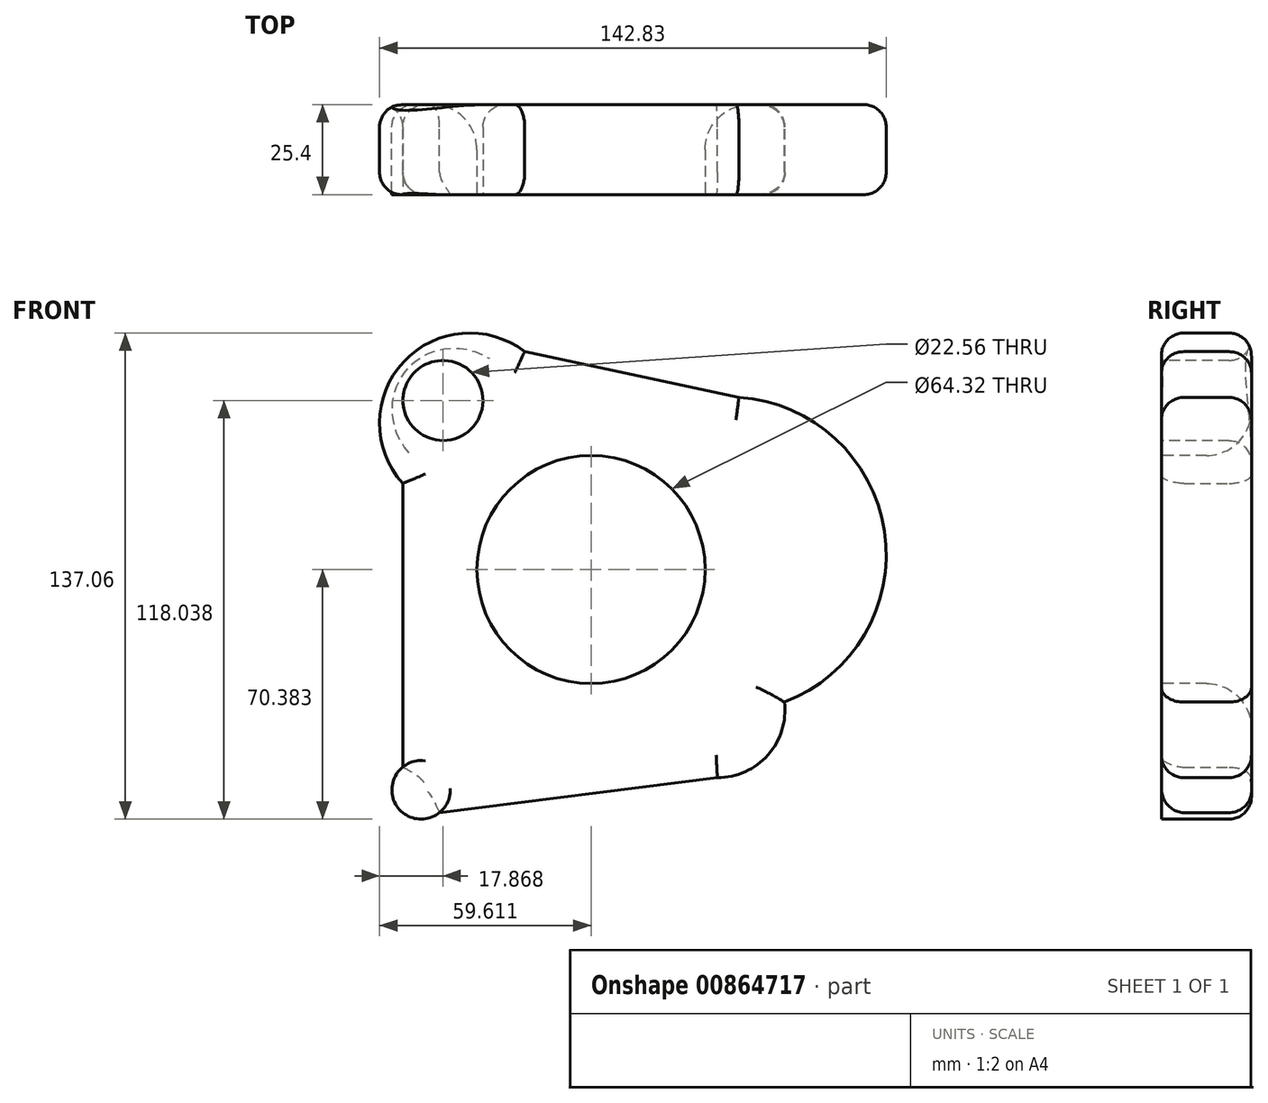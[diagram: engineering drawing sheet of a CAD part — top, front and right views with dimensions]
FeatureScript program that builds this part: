
annotation { "Feature Type Name" : "Feature", "Feature Type Description" : "" }
export const myFeature = defineFeature(function(context is Context, id is Id, definition is map)
    precondition{}
    {
        {
            var Q0;
            Q0=qCreatedBy(makeId("Front.planeOp"),FACE);
            var sketch = newSketch(context, id + "F0", { "sketchPlane" : qUnion([Q0])});
            skCircle(sketch, "E0", {"center": v(-53.98, 60.28) * mm, "radius": 25.4 * mm});
            skCircle(sketch, "E1", {"center": v(19, 23.17) * mm, "radius": 44.45 * mm});
            skCircle(sketch, "E2", {"center": v(-67.66, -43.13) * mm, "radius": 8.26 * mm});
            skCircle(sketch, "E3", {"center": v(15.86, -20.64) * mm, "radius": 19.05 * mm});
            skLineSegment(sketch, "E4", {"start": v(-38.48, 80.4) * mm, "end": v(34.4, 64.86) * mm});
            skLineSegment(sketch, "E5", {"start": v(60.44, 7.1) * mm, "end": v(15.86, -20.64) * mm});
            skLineSegment(sketch, "E6", {"start": v(15.86, -39.7) * mm, "end": v(-62.46, -49.54) * mm});
            skLineSegment(sketch, "E7", {"start": v(-72.86, 43.3) * mm, "end": v(-72.86, -36.72) * mm});
            skSolve(sketch);
        }
        {
            var Q0;
            Q0 = qSketchRegion(id + "F0", true);
            extrude(context, id + "F1", {"entities" : qUnion([Q0]), "depth" : 25.4 * mm, "offsetDistance" : 25.4 * mm});
        }
        {
            var Q0;
            Q0=makeQuery(id+"F1.opExtrude","CAP_FACE",FACE,{"disambiguationData":[OSD([sQuery(id+"F0.wireOp",EDGE,"E0"),sQuery(id+"F0.wireOp",EDGE,"E1"),sQuery(id+"F0.wireOp",EDGE,"E2"),sQuery(id+"F0.wireOp",EDGE,"E3"),sQuery(id+"F0.wireOp",EDGE,"E4"),sQuery(id+"F0.wireOp",EDGE,"E6"),sQuery(id+"F0.wireOp",EDGE,"E7")])],"isStart":false});
            var sketch = newSketch(context, id + "F2", { "sketchPlane" : qUnion([Q0])});
            skCircle(sketch, "E8", {"center": v(-61.51, 66.66) * mm, "radius": 11.28 * mm});
            skSolve(sketch);
        }
        {
            var Q0;
            Q0 = qSketchRegion(id + "F2", true);
            extrude(context, id + "F3", {"entities" : qUnion([Q0]), "operationType" : NewBodyOperationType.ADD, "depth" : 76.2 * mm, "offsetDistance" : 25.4 * mm});
        }
        {
            var Q0;
            Q0=makeQuery(id+"F3.opExtrude","CAP_FACE",FACE,{"disambiguationData":[OSD([sQuery(id+"F2.wireOp",EDGE,"E8")])],"isStart":false});
            extrude(context, id + "F4", {"entities" : qUnion([Q0]), "operationType" : NewBodyOperationType.REMOVE, "endBound" : BoundingType.THROUGH_ALL, "oppositeDirection" : true, "depth" : 25.4 * mm, "offsetDistance" : 25.4 * mm});
        }
        {
            var Q0;
            Q0=makeQuery(id+"Fvwkc0aiCjp0DBf_1.boolean.opBoolean","INTERSECT",EDGE,{"derivedFrom":[makeQuery(id+"F1.opExtrude","CAP_FACE",FACE,{"disambiguationData":[OSD([sQuery(id+"F0.wireOp",EDGE,"E0"),sQuery(id+"F0.wireOp",EDGE,"E1"),sQuery(id+"F0.wireOp",EDGE,"E2"),sQuery(id+"F0.wireOp",EDGE,"E3"),sQuery(id+"F0.wireOp",EDGE,"E4"),sQuery(id+"F0.wireOp",EDGE,"E6"),sQuery(id+"F0.wireOp",EDGE,"E7")])],"isStart":true}),makeQuery(id+"Fvwkc0aiCjp0DBf_1.opExtrude","SWEPT_FACE",FACE,{"disambiguationData":[OSD([sQuery(id+"FM4Ox1MiRYVjufH_1.wireOp",EDGE,"iZuMQ9Cg-E2lU-WlAJ-14QO-pkKDaHSdI4NP.left")])]})]});
            var Q1;
            Q1=makeQuery(id+"Fvwkc0aiCjp0DBf_1.boolean.opBoolean","INTERSECT",EDGE,{"derivedFrom":[makeQuery(id+"F1.opExtrude","CAP_FACE",FACE,{"disambiguationData":[OSD([sQuery(id+"F0.wireOp",EDGE,"E0"),sQuery(id+"F0.wireOp",EDGE,"E1"),sQuery(id+"F0.wireOp",EDGE,"E2"),sQuery(id+"F0.wireOp",EDGE,"E3"),sQuery(id+"F0.wireOp",EDGE,"E4"),sQuery(id+"F0.wireOp",EDGE,"E6"),sQuery(id+"F0.wireOp",EDGE,"E7")])],"isStart":true}),makeQuery(id+"Fvwkc0aiCjp0DBf_1.opExtrude","SWEPT_FACE",FACE,{"disambiguationData":[OSD([sQuery(id+"FM4Ox1MiRYVjufH_1.wireOp",EDGE,"iZuMQ9Cg-E2lU-WlAJ-14QO-pkKDaHSdI4NP.top")])]})]});
            var Q2;
            Q2=makeQuery(id+"F1.opExtrude","CAP_FACE",FACE,{"disambiguationData":[OSD([sQuery(id+"F0.wireOp",EDGE,"E0"),sQuery(id+"F0.wireOp",EDGE,"E1"),sQuery(id+"F0.wireOp",EDGE,"E2"),sQuery(id+"F0.wireOp",EDGE,"E3"),sQuery(id+"F0.wireOp",EDGE,"E4"),sQuery(id+"F0.wireOp",EDGE,"E6"),sQuery(id+"F0.wireOp",EDGE,"E7")])],"isStart":true});
            var Q3;
            Q3=makeQuery(id+"Fvwkc0aiCjp0DBf_1.boolean.opBoolean","INTERSECT",EDGE,{"derivedFrom":[makeQuery(id+"F1.opExtrude","CAP_FACE",FACE,{"disambiguationData":[OSD([sQuery(id+"F0.wireOp",EDGE,"E0"),sQuery(id+"F0.wireOp",EDGE,"E1"),sQuery(id+"F0.wireOp",EDGE,"E2"),sQuery(id+"F0.wireOp",EDGE,"E3"),sQuery(id+"F0.wireOp",EDGE,"E4"),sQuery(id+"F0.wireOp",EDGE,"E6"),sQuery(id+"F0.wireOp",EDGE,"E7")])],"isStart":true}),makeQuery(id+"Fvwkc0aiCjp0DBf_1.opExtrude","SWEPT_FACE",FACE,{"disambiguationData":[OSD([sQuery(id+"FM4Ox1MiRYVjufH_1.wireOp",EDGE,"iZuMQ9Cg-E2lU-WlAJ-14QO-pkKDaHSdI4NP.bottom")])]})]});
            var Q4;
            Q4=makeQuery(id+"Fvwkc0aiCjp0DBf_1.boolean.opBoolean","INTERSECT",EDGE,{"derivedFrom":[makeQuery(id+"F1.opExtrude","CAP_FACE",FACE,{"disambiguationData":[OSD([sQuery(id+"F0.wireOp",EDGE,"E0"),sQuery(id+"F0.wireOp",EDGE,"E1"),sQuery(id+"F0.wireOp",EDGE,"E2"),sQuery(id+"F0.wireOp",EDGE,"E3"),sQuery(id+"F0.wireOp",EDGE,"E4"),sQuery(id+"F0.wireOp",EDGE,"E6"),sQuery(id+"F0.wireOp",EDGE,"E7")])],"isStart":true}),makeQuery(id+"Fvwkc0aiCjp0DBf_1.opExtrude","SWEPT_FACE",FACE,{"disambiguationData":[OSD([sQuery(id+"FM4Ox1MiRYVjufH_1.wireOp",EDGE,"iZuMQ9Cg-E2lU-WlAJ-14QO-pkKDaHSdI4NP.right")])]})]});
            var Q5;
            Q5=makeQuery(id+"F1.opExtrude","CAP_EDGE",EDGE,{"disambiguationData":[OSD([sQuery(id+"F0.wireOp",EDGE,"E6")])],"isStart":false});
            var Q6;
            Q6=makeQuery(id+"F1.opExtrude","CAP_EDGE",EDGE,{"disambiguationData":[OSD([sQuery(id+"F0.wireOp",EDGE,"E3")])],"isStart":false});
            var Q7;
            Q7=makeQuery(id+"F1.opExtrude","CAP_EDGE",EDGE,{"disambiguationData":[OSD([sQuery(id+"F0.wireOp",EDGE,"E1")])],"isStart":false});
            var Q8;
            Q8=makeQuery(id+"F1.opExtrude","CAP_EDGE",EDGE,{"disambiguationData":[OSD([sQuery(id+"F0.wireOp",EDGE,"E4")])],"isStart":false});
            var Q9;
            Q9=makeQuery(id+"F1.opExtrude","CAP_EDGE",EDGE,{"disambiguationData":[OSD([sQuery(id+"F0.wireOp",EDGE,"E0")])],"isStart":false});
            var Q10;
            Q10=makeQuery(id+"F1.opExtrude","CAP_EDGE",EDGE,{"disambiguationData":[OSD([sQuery(id+"F0.wireOp",EDGE,"E7")])],"isStart":false});
            var Q11;
            Q11=makeQuery(id+"F3.opExtrude","CAP_EDGE",EDGE,{"disambiguationData":[OSD([sQuery(id+"F2.wireOp",EDGE,"E8")])],"isStart":true});
            fillet(context, id + "F5", {"entities" : qUnion([Q0, Q1, Q2, Q3, Q4, Q5, Q6, Q7, Q8, Q9, Q10, Q11]), "radius" : 6.35 * mm, "tangentPropagation" : true, "allowEdgeOverflow" : false});
        }
        {
            var Q0;
            Q0=makeQuery(id+"F1.opExtrude","CAP_FACE",FACE,{"disambiguationData":[OSD([sQuery(id+"F0.wireOp",EDGE,"E0"),sQuery(id+"F0.wireOp",EDGE,"E1"),sQuery(id+"F0.wireOp",EDGE,"E2"),sQuery(id+"F0.wireOp",EDGE,"E3"),sQuery(id+"F0.wireOp",EDGE,"E4"),sQuery(id+"F0.wireOp",EDGE,"E6"),sQuery(id+"F0.wireOp",EDGE,"E7")])],"isStart":false});
            var sketch = newSketch(context, id + "F6", { "sketchPlane" : qUnion([Q0])});
            skCircle(sketch, "E9", {"center": v(-19.77, 19) * mm, "radius": 32.16 * mm});
            skSolve(sketch);
        }
        {
            var Q0;
            Q0=makeQuery(id+"F6.imprint","IMPRINT",FACE,{"disambiguationData":[TD([[makeQuery(id+"F6.imprint","IMPRINT",EDGE,{"derivedFrom":sQuery(id+"F6.wireOp",EDGE,"E9")}),1.0]])]});
            extrude(context, id + "F7", {"entities" : qUnion([Q0]), "operationType" : NewBodyOperationType.REMOVE, "endBound" : BoundingType.THROUGH_ALL, "oppositeDirection" : true, "depth" : 25.4 * mm, "offsetDistance" : 25.4 * mm});
        }
        {
            var Q0;
            Q0=makeQuery(id+"F7.boolean.opBoolean","COPY",EDGE,{"derivedFrom":makeQuery(id+"F7.opExtrude","CAP_EDGE",EDGE,{"disambiguationData":[OSD([sQuery(id+"F6.wireOp",EDGE,"E9")])],"isStart":true})});
            var Q1;
            Q1=makeQuery(id+"F7.boolean.opBoolean","INTERSECT",EDGE,{"derivedFrom":[makeQuery(id+"F1.opExtrude","CAP_FACE",FACE,{"disambiguationData":[OSD([sQuery(id+"F0.wireOp",EDGE,"E0"),sQuery(id+"F0.wireOp",EDGE,"E1"),sQuery(id+"F0.wireOp",EDGE,"E2"),sQuery(id+"F0.wireOp",EDGE,"E3"),sQuery(id+"F0.wireOp",EDGE,"E4"),sQuery(id+"F0.wireOp",EDGE,"E6"),sQuery(id+"F0.wireOp",EDGE,"E7")])],"isStart":true}),makeQuery(id+"F7.opExtrude","SWEPT_FACE",FACE,{"disambiguationData":[OSD([sQuery(id+"F6.wireOp",EDGE,"E9")])]})]});
            fillet(context, id + "F8", {"entities" : qUnion([Q0, Q1]), "radius" : 12.7 * mm, "tangentPropagation" : true, "allowEdgeOverflow" : false});
        }
    });
